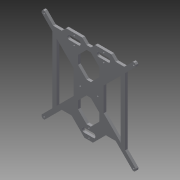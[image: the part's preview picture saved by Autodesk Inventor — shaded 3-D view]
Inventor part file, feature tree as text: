
AUTODESK INVENTOR PART (.ipt)
format: ipt  version: 2015 (Build 190159000, 159)  size: 273,920 bytes
history: native  units: mm
features: chamfer x4, sketch x4, extrude x3, hole x1
ambient origin geometry x8: Origin, YZ Plane, XZ Plane, XY Plane, X Axis, Y Axis, Z Axis, Center Point
bodies: Solid1 (feature_tree)
feature tree (12):
  extrude  "Extrusion1"  Depth=220.0mm
  extrude  "Extrusion2"  Depth=6.0mm
  chamfer  "Chamfer3"  Distance=7.0mm
  chamfer  "Chamfer4"  Distance=10.0mm
  chamfer  "Chamfer5"  Distance=40.0mm
  chamfer  "Chamfer6"  Angle=135.0deg  [1 undecoded]
  extrude  "Extrusion3"  Depth=4.0mm
  hole  "Hole1"  [1 undecoded]
  sketch  "Sketch1"  dims[d0=220.0mm d1=220.0mm]
  sketch  "Sketch2"  dims[d2=6.0mm d3=0.0mm d4=206.0mm]
  sketch  "Sketch3"  dims[d6=25.0mm]
  sketch  "Sketch4"  dims[d7=135.0deg d8=7.0mm d10=10.0mm d11=40.0mm d12=135.0deg d13=7.0mm d14=20.0mm d15=135.0deg d16=38.0mm d17=10.0mm d20=25.0mm d21=60.0mm d22=10.0mm d23=135.0deg d24=57.0mm d25=7.0mm d26=40.0mm d27=10.0mm d28=30.0mm d29=0.0mm d30=0.0mm d37=3.0mm d38=4.0mm d39=45.0deg d40=3.0mm d41=4.0mm d42=45.0deg d43=3.0mm d44=4.0mm d45=45.0deg d46=3.0mm d47=4.0mm d48=45.0deg d50=10.0mm d51=31.0mm d52=10.0mm d56=4.0mm d57=4.0mm d58=10.0mm d60=14.0mm d61=6.0mm d62=0.0mm d63=5.0mm d64=5.0mm d65=5.0mm d66=5.0mm d67=5.0mm d68=11.5mm d69=20.49mm d70=20.037mm d71=5.642mm d72=5.642mm d73=5.0mm d74=3.6mm d75=6.0mm d76=4.0mm d77=2.0mm d78=90.0deg d79=8.0mm d80=20.594885mm]
note: 2 required parameter values undecoded (feature->parameter linkage not recoverable at this tier; creation-order binding heuristic only, values carry confidence <= 0.55)
